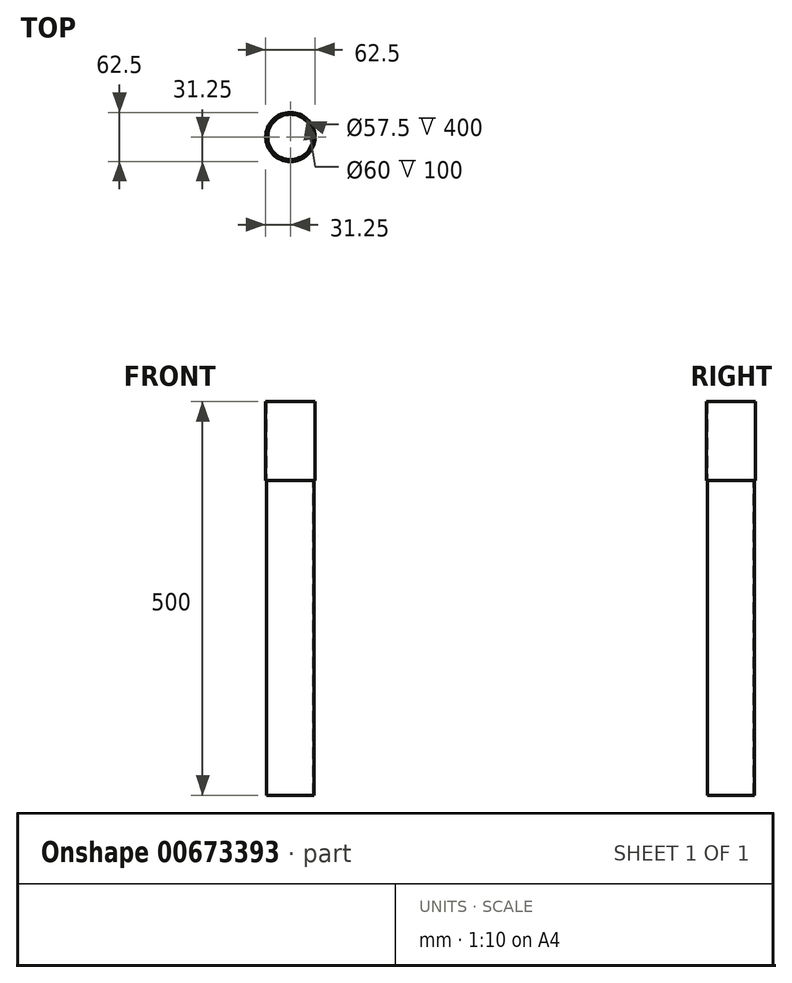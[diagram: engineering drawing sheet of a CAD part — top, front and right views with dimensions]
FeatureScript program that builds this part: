
annotation { "Feature Type Name" : "Feature", "Feature Type Description" : "" }
export const myFeature = defineFeature(function(context is Context, id is Id, definition is map)
    precondition{}
    {
        {
            var Q0;
            Q0=qCreatedBy(makeId("Top.planeOp"),FACE);
            var sketch = newSketch(context, id + "F0", { "sketchPlane" : qUnion([Q0])});
            skCircle(sketch, "E0", {"center": v(0, 0) * mm, "radius": 31.25 * mm});
            skCircle(sketch, "E1", {"center": v(0, 0) * mm, "radius": 30 * mm});
            skSolve(sketch);
        }
        {
            var Q0;
            Q0=makeQuery(id+"F0.imprint","IMPRINT",FACE,{"disambiguationData":[TD([[makeQuery(id+"F0.imprint","IMPRINT",EDGE,{"derivedFrom":sQuery(id+"F0.wireOp",EDGE,"E0")}),1.0]])]});
            var Q1;
            Q1=sQuery(id+"F0.wireOp",EDGE,"E1");
            var Q2;
            Q2=sQuery(id+"F0.wireOp",EDGE,"E0");
            extrude(context, id + "F1", {"entities" : qUnion([Q0]), "surfaceEntities" : qUnion([Q1, Q2]), "depth" : 100 * mm, "offsetDistance" : 25 * mm});
        }
        {
            var Q0;
            Q0=qCreatedBy(makeId("Top.planeOp"),FACE);
            var sketch = newSketch(context, id + "F2", { "sketchPlane" : qUnion([Q0])});
            skCircle(sketch, "E2", {"center": v(0, 0) * mm, "radius": 28.75 * mm});
            skCircle(sketch, "E3", {"center": v(0, 0) * mm, "radius": 30 * mm});
            skSolve(sketch);
        }
        {
            var Q0;
            Q0 = qSketchRegion(id + "F2", true);
            extrude(context, id + "F3", {"entities" : qUnion([Q0]), "oppositeDirection" : true, "depth" : 400 * mm, "offsetDistance" : 25 * mm});
        }
    });
